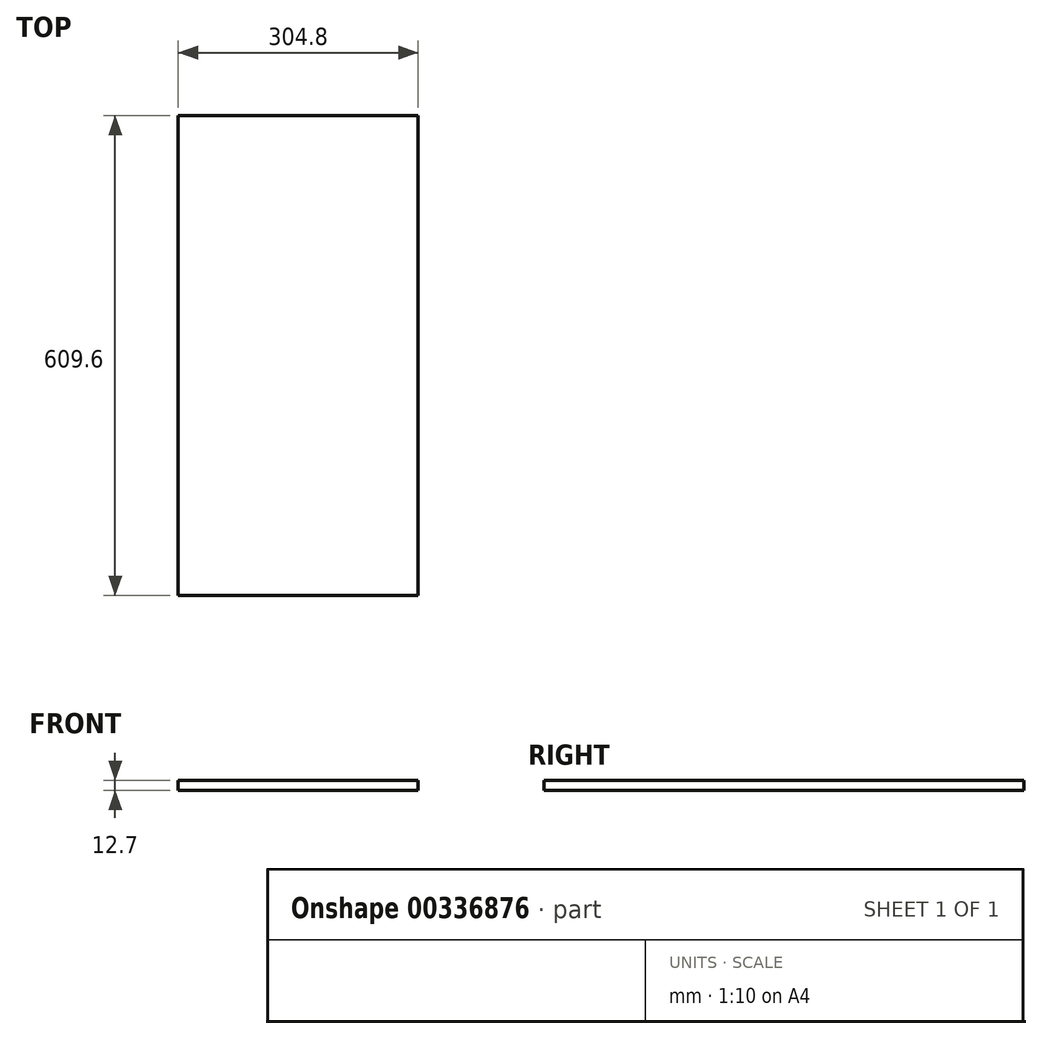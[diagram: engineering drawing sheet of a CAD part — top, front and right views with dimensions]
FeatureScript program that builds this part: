
annotation { "Feature Type Name" : "Feature", "Feature Type Description" : "" }
export const myFeature = defineFeature(function(context is Context, id is Id, definition is map)
    precondition{}
    {
        {
            var Q0;
            Q0=qCreatedBy(makeId("Right.planeOp"),FACE);
            var sketch = newSketch(context, id + "F0", { "sketchPlane" : qUnion([Q0])});
            skLineSegment(sketch, "E0.bottom", {"start": v(-36.13, 43.18) * mm, "end": v(573.47, 43.18) * mm});
            skLineSegment(sketch, "E0.top", {"start": v(-36.13, 30.48) * mm, "end": v(573.47, 30.48) * mm});
            skLineSegment(sketch, "E0.left", {"start": v(-36.13, 43.18) * mm, "end": v(-36.13, 30.48) * mm});
            skLineSegment(sketch, "E0.right", {"start": v(573.47, 43.18) * mm, "end": v(573.47, 30.48) * mm});
            skSolve(sketch);
        }
        {
            var Q0;
            Q0=makeQuery(id+"F0.imprint","IMPRINT",FACE,{"disambiguationData":[TD([[makeQuery(id+"F0.imprint","IMPRINT",EDGE,{"derivedFrom":sQuery(id+"F0.wireOp",EDGE,"E0.bottom")}),-1.0]])]});
            extrude(context, id + "F1", {"entities" : qUnion([Q0]), "depth" : 304.8 * mm});
        }
    });
